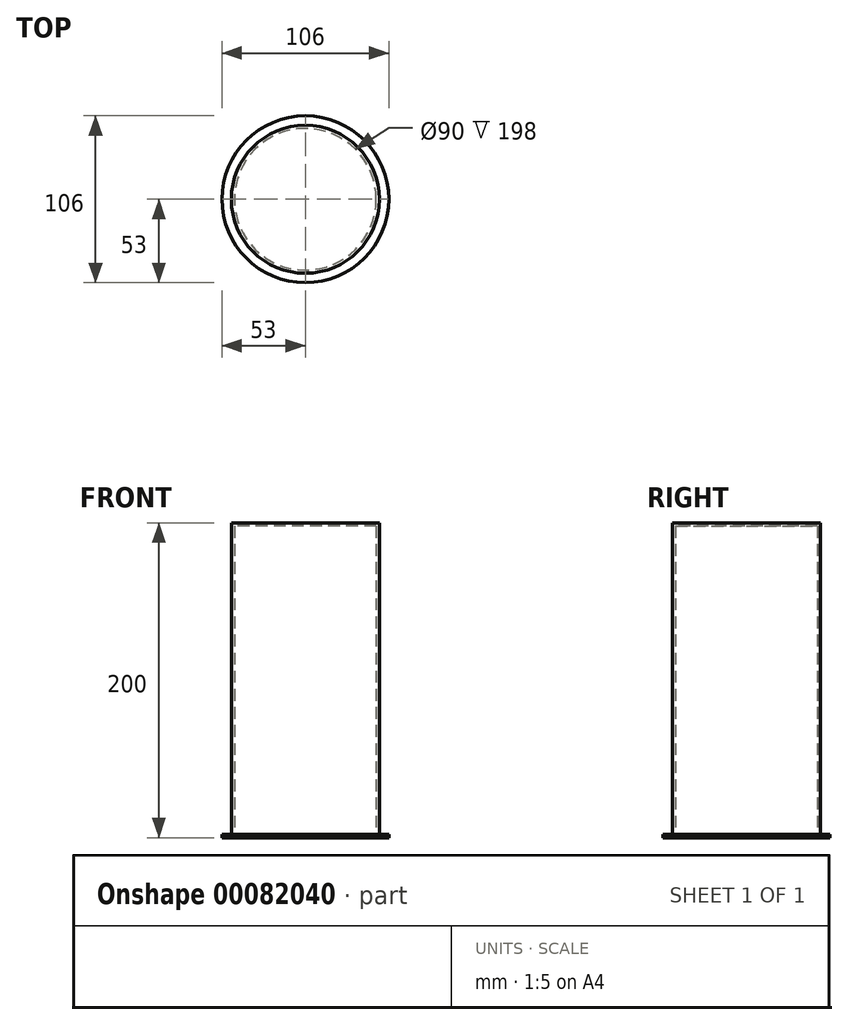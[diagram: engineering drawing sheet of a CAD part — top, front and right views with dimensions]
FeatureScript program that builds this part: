
annotation { "Feature Type Name" : "Feature", "Feature Type Description" : "" }
export const myFeature = defineFeature(function(context is Context, id is Id, definition is map)
    precondition{}
    {
        {
            var Q0;
            Q0=qCreatedBy(makeId("Top.planeOp"),FACE);
            var sketch = newSketch(context, id + "F0", { "sketchPlane" : qUnion([Q0])});
            skCircle(sketch, "E0", {"center": v(0, 0) * mm, "radius": 53 * mm});
            skCircle(sketch, "E1", {"center": v(0, 0) * mm, "radius": 47 * mm});
            skSolve(sketch);
        }
        {
            var Q0;
            Q0=makeQuery(id+"F0.imprint","IMPRINT",FACE,{"disambiguationData":[TD([[makeQuery(id+"F0.imprint","IMPRINT",EDGE,{"derivedFrom":sQuery(id+"F0.wireOp",EDGE,"E0")}),1.0]])]});
            extrude(context, id + "F1", {"entities" : qUnion([Q0]), "depth" : 2 * mm});
        }
        {
            var Q0;
            Q0=makeQuery(id+"F0.imprint","IMPRINT",FACE,{"disambiguationData":[TD([[makeQuery(id+"F0.imprint","IMPRINT",EDGE,{"derivedFrom":sQuery(id+"F0.wireOp",EDGE,"E1")}),1.0]])]});
            extrude(context, id + "F2", {"entities" : qUnion([Q0]), "operationType" : NewBodyOperationType.ADD, "depth" : 200 * mm});
        }
        {
            var Q0;
            {var subQ0=sQuery(id+"F0.wireOp",EDGE,"E1");Q0=makeQuery(id+"F2.boolean.opBoolean","MERGE",FACE,{"derivedFrom":[makeQuery(id+"F1.opExtrude","CAP_FACE",FACE,{"disambiguationData":[OSD([sQuery(id+"F0.wireOp",EDGE,"E0"),subQ0])],"isStart":true}),makeQuery(id+"F2.opExtrude","CAP_FACE",FACE,{"disambiguationData":[OSD([subQ0])],"isStart":true})]});}
            shell(context, id + "F3", {"entities" : qUnion([Q0]), "thickness" : 2 * mm});
        }
    });
